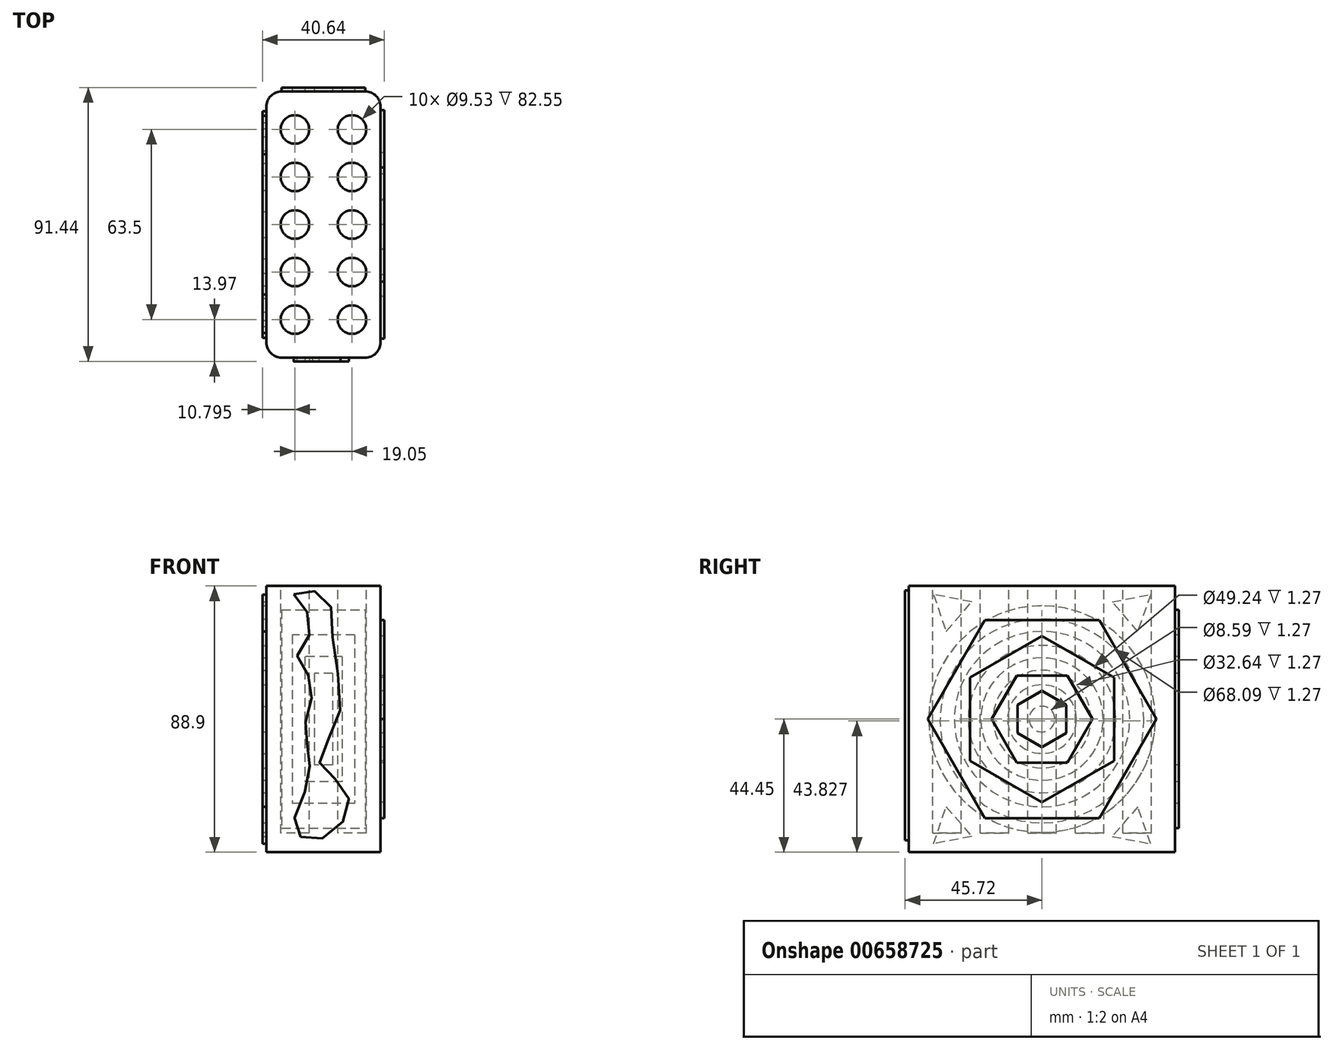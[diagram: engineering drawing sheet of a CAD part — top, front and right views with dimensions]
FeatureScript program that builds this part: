
annotation { "Feature Type Name" : "Feature", "Feature Type Description" : "" }
export const myFeature = defineFeature(function(context is Context, id is Id, definition is map)
    precondition{}
    {
        {
            var Q0;
            Q0=qCreatedBy(makeId("Right.planeOp"),FACE);
            var sketch = newSketch(context, id + "F0", { "sketchPlane" : qUnion([Q0])});
            skLineSegment(sketch, "E0.bottom", {"start": v(-44.45, 44.45) * mm, "end": v(44.45, 44.45) * mm});
            skLineSegment(sketch, "E0.top", {"start": v(-44.45, -44.45) * mm, "end": v(44.45, -44.45) * mm});
            skLineSegment(sketch, "E0.left", {"start": v(-44.45, 44.45) * mm, "end": v(-44.45, -44.45) * mm});
            skLineSegment(sketch, "E0.right", {"start": v(44.45, 44.45) * mm, "end": v(44.45, -44.45) * mm});
            skPoint(sketch, "E0.middle", {"position": v(0, 0) * mm});
            skSolve(sketch);
        }
        {
            var Q0;
            Q0=qSketchRegion(id+"F0",true);
            extrude(context, id + "F1", {"entities" : qUnion([Q0]), "endBound" : BoundingType.SYMMETRIC, "depth" : 38.1 * mm, "offsetDistance" : 25.4 * mm});
        }
        {
            var Q0;
            Q0=makeQuery(id+"F1.opExtrude","SWEPT_FACE",FACE,{"disambiguationData":[OSD([sQuery(id+"F0.wireOp",EDGE,"E0.bottom")])]});
            var sketch = newSketch(context, id + "F2", { "sketchPlane" : qUnion([Q0])});
            skCircle(sketch, "E1", {"center": v(-9.52, -31.75) * mm, "radius": 4.76 * mm});
            skCircle(sketch, "E2", {"center": v(-9.52, 0) * mm, "radius": 4.76 * mm});
            skCircle(sketch, "E3", {"center": v(-9.52, -15.88) * mm, "radius": 4.76 * mm});
            skCircle(sketch, "E4", {"center": v(-9.52, 15.88) * mm, "radius": 4.76 * mm});
            skCircle(sketch, "E5", {"center": v(-9.52, 31.75) * mm, "radius": 4.76 * mm});
            skCircle(sketch, "E6.MirrorC", {"center": v(9.52, 0) * mm, "radius": 4.76 * mm});
            skCircle(sketch, "E7.MirrorC", {"center": v(9.52, -31.75) * mm, "radius": 4.76 * mm});
            skCircle(sketch, "E8.MirrorC", {"center": v(9.52, -15.88) * mm, "radius": 4.76 * mm});
            skCircle(sketch, "E9.MirrorC", {"center": v(9.52, 15.88) * mm, "radius": 4.76 * mm});
            skCircle(sketch, "E10.MirrorC", {"center": v(9.52, 31.75) * mm, "radius": 4.76 * mm});
            skSolve(sketch);
        }
        {
            var Q0;
            Q0=qSketchRegion(id+"F2",true);
            extrude(context, id + "F3", {"entities" : qUnion([Q0]), "operationType" : NewBodyOperationType.REMOVE, "oppositeDirection" : true, "depth" : 82.55 * mm, "offsetDistance" : 25.4 * mm});
        }
        {
            var Q0;
            Q0=makeQuery(id+"F1.opExtrude","CAP_EDGE",EDGE,{"disambiguationData":[OSD([sQuery(id+"F0.wireOp",EDGE,"E0.left")])],"isStart":false});
            var Q1;
            Q1=makeQuery(id+"F1.opExtrude","CAP_EDGE",EDGE,{"disambiguationData":[OSD([sQuery(id+"F0.wireOp",EDGE,"E0.right")])],"isStart":false});
            var Q2;
            Q2=makeQuery(id+"F1.opExtrude","CAP_EDGE",EDGE,{"disambiguationData":[OSD([sQuery(id+"F0.wireOp",EDGE,"E0.right")])],"isStart":true});
            var Q3;
            Q3=makeQuery(id+"F1.opExtrude","CAP_EDGE",EDGE,{"disambiguationData":[OSD([sQuery(id+"F0.wireOp",EDGE,"E0.left")])],"isStart":true});
            fillet(context, id + "F4", {"entities" : qUnion([Q0, Q1, Q2, Q3]), "radius" : 5.08 * mm, "tangentPropagation" : true, "allowEdgeOverflow" : false});
        }
        {
            var Q0;
            Q0=makeQuery(id+"F1.opExtrude","CAP_FACE",FACE,{"disambiguationData":[OSD([sQuery(id+"F0.wireOp",EDGE,"E0.bottom"),sQuery(id+"F0.wireOp",EDGE,"E0.top"),sQuery(id+"F0.wireOp",EDGE,"E0.left"),sQuery(id+"F0.wireOp",EDGE,"E0.right")])],"isStart":false});
            var sketch = newSketch(context, id + "F5", { "sketchPlane" : qUnion([Q0])});
            skCircle(sketch, "E11.cCircle", {"center": v(0, 0) * mm, "radius": 8.15 * mm, "construction": true});
            skLineSegment(sketch, "E11.0", {"start": v(-8.15, -4.7) * mm, "end": v(-8.15, 4.7) * mm});
            skLineSegment(sketch, "E11.1", {"start": v(-8.15, 4.7) * mm, "end": v(0, 9.4) * mm});
            skLineSegment(sketch, "E11.2", {"start": v(0, 9.4) * mm, "end": v(8.15, 4.7) * mm});
            skLineSegment(sketch, "E11.3", {"start": v(8.15, 4.7) * mm, "end": v(8.15, -4.7) * mm});
            skLineSegment(sketch, "E11.4", {"start": v(8.15, -4.7) * mm, "end": v(0, -9.4) * mm});
            skLineSegment(sketch, "E11.5", {"start": v(0, -9.4) * mm, "end": v(-8.15, -4.7) * mm});
            skPoint(sketch, "E11.0.midPoint", {"position": v(-8.15, 0) * mm});
            skCircle(sketch, "E12.cCircle", {"center": v(0, 0) * mm, "radius": 14.58 * mm, "construction": true});
            skLineSegment(sketch, "E12.0", {"start": v(8.42, -14.58) * mm, "end": v(-8.42, -14.58) * mm});
            skLineSegment(sketch, "E12.1", {"start": v(-8.42, -14.58) * mm, "end": v(-16.84, 0) * mm});
            skLineSegment(sketch, "E12.2", {"start": v(-16.84, 0) * mm, "end": v(-8.42, 14.58) * mm});
            skLineSegment(sketch, "E12.3", {"start": v(-8.42, 14.58) * mm, "end": v(8.42, 14.58) * mm});
            skLineSegment(sketch, "E12.4", {"start": v(8.42, 14.58) * mm, "end": v(16.84, 0) * mm});
            skLineSegment(sketch, "E12.5", {"start": v(16.84, 0) * mm, "end": v(8.42, -14.58) * mm});
            skPoint(sketch, "E12.0.midPoint", {"position": v(0, -14.58) * mm});
            skCircle(sketch, "E13.cCircle", {"center": v(0, 0) * mm, "radius": 24.04 * mm, "construction": true});
            skLineSegment(sketch, "E13.0", {"start": v(-24.04, -13.88) * mm, "end": v(-24.04, 13.88) * mm});
            skLineSegment(sketch, "E13.1", {"start": v(-24.04, 13.88) * mm, "end": v(0, 27.76) * mm});
            skLineSegment(sketch, "E13.2", {"start": v(0, 27.76) * mm, "end": v(24.04, 13.88) * mm});
            skLineSegment(sketch, "E13.3", {"start": v(24.04, 13.88) * mm, "end": v(24.04, -13.88) * mm});
            skLineSegment(sketch, "E13.4", {"start": v(24.04, -13.88) * mm, "end": v(0, -27.76) * mm});
            skLineSegment(sketch, "E13.5", {"start": v(0, -27.76) * mm, "end": v(-24.04, -13.88) * mm});
            skPoint(sketch, "E13.0.midPoint", {"position": v(-24.04, 0) * mm});
            skCircle(sketch, "E14.cCircle", {"center": v(0, 0) * mm, "radius": 33.06 * mm, "construction": true});
            skLineSegment(sketch, "E14.0", {"start": v(19.08, -33.06) * mm, "end": v(-19.08, -33.06) * mm});
            skLineSegment(sketch, "E14.1", {"start": v(-19.08, -33.06) * mm, "end": v(-38.17, 0) * mm});
            skLineSegment(sketch, "E14.2", {"start": v(-38.17, 0) * mm, "end": v(-19.08, 33.06) * mm});
            skLineSegment(sketch, "E14.3", {"start": v(-19.08, 33.06) * mm, "end": v(19.08, 33.06) * mm});
            skLineSegment(sketch, "E14.4", {"start": v(19.08, 33.06) * mm, "end": v(38.17, 0) * mm});
            skLineSegment(sketch, "E14.5", {"start": v(38.17, 0) * mm, "end": v(19.08, -33.06) * mm});
            skPoint(sketch, "E14.0.midPoint", {"position": v(0, -33.06) * mm});
            skSolve(sketch);
        }
        {
            var Q0;
            Q0=makeQuery(id+"F5.imprint","IMPRINT",FACE,{"disambiguationData":[TD([[makeQuery(id+"F5.imprint","IMPRINT",EDGE,{"derivedFrom":sQuery(id+"F5.wireOp",EDGE,"E11.0")}),1.0]])]});
            var Q1;
            Q1=makeQuery(id+"F5.imprint","IMPRINT",FACE,{"disambiguationData":[TD([[makeQuery(id+"F5.imprint","IMPRINT",EDGE,{"derivedFrom":sQuery(id+"F5.wireOp",EDGE,"E13.0")}),1.0]])]});
            extrude(context, id + "F6", {"entities" : qUnion([Q0, Q1]), "operationType" : NewBodyOperationType.ADD, "depth" : 1.27 * mm, "offsetDistance" : 25.4 * mm});
        }
        {
            var Q0;
            Q0=makeQuery(id+"F1.opExtrude","CAP_FACE",FACE,{"disambiguationData":[OSD([sQuery(id+"F0.wireOp",EDGE,"E0.bottom"),sQuery(id+"F0.wireOp",EDGE,"E0.top"),sQuery(id+"F0.wireOp",EDGE,"E0.left"),sQuery(id+"F0.wireOp",EDGE,"E0.right")])],"isStart":true});
            var sketch = newSketch(context, id + "F7", { "sketchPlane" : qUnion([Q0])});
            skCircle(sketch, "E15", {"center": v(0, 0) * mm, "radius": 4.3 * mm});
            skCircle(sketch, "E16", {"center": v(0, 0) * mm, "radius": 11.47 * mm});
            skCircle(sketch, "E17", {"center": v(0, 0) * mm, "radius": 16.32 * mm});
            skCircle(sketch, "E18", {"center": v(0, 0) * mm, "radius": 20.43 * mm});
            skCircle(sketch, "E19", {"center": v(0, 0) * mm, "radius": 24.62 * mm});
            skCircle(sketch, "E20", {"center": v(0, 0) * mm, "radius": 29.27 * mm});
            skCircle(sketch, "E21", {"center": v(0, -0.62) * mm, "radius": 34.04 * mm});
            skCircle(sketch, "E22", {"center": v(0, 0) * mm, "radius": 37.84 * mm});
            skSolve(sketch);
        }
        {
            var Q0;
            Q0=makeQuery(id+"F7.imprint","IMPRINT",FACE,{"disambiguationData":[TD([[makeQuery(id+"F7.imprint","IMPRINT",EDGE,{"derivedFrom":sQuery(id+"F7.wireOp",EDGE,"E15")}),-1.0]])]});
            var Q1;
            Q1=makeQuery(id+"F7.imprint","IMPRINT",FACE,{"disambiguationData":[TD([[makeQuery(id+"F7.imprint","IMPRINT",EDGE,{"derivedFrom":sQuery(id+"F7.wireOp",EDGE,"E17")}),-1.0]])]});
            var Q2;
            Q2=makeQuery(id+"F7.imprint","IMPRINT",FACE,{"disambiguationData":[TD([[makeQuery(id+"F7.imprint","IMPRINT",EDGE,{"derivedFrom":sQuery(id+"F7.wireOp",EDGE,"E19")}),-1.0]])]});
            var Q3;
            Q3=makeQuery(id+"F7.imprint","IMPRINT",FACE,{"disambiguationData":[TD([[makeQuery(id+"F7.imprint","IMPRINT",EDGE,{"derivedFrom":sQuery(id+"F7.wireOp",EDGE,"E21")}),-1.0]])]});
            extrude(context, id + "F8", {"entities" : qUnion([Q0, Q1, Q2, Q3]), "operationType" : NewBodyOperationType.ADD, "depth" : 1.27 * mm, "offsetDistance" : 25.4 * mm});
        }
        {
            var Q0;
            {var subQ0=sQuery(id+"F0.wireOp",EDGE,"E0.right");var subQ1=sQuery(id+"F0.wireOp",EDGE,"E0.bottom");var subQ2=sQuery(id+"F0.wireOp",EDGE,"E0.top");var subQ3=sQuery(id+"F0.wireOp",EDGE,"E0.left");Q0=makeQuery(id+"F8.boolean.opBoolean","SPLIT",FACE,{"disambiguationData":[TD([makeQuery(id+"F1.opExtrude","SWEPT_FACE",FACE,{"disambiguationData":[OSD([subQ1])]})])],"derivedFrom":makeQuery(id+"F1.opExtrude","CAP_FACE",FACE,{"disambiguationData":[OSD([subQ1,subQ2,subQ3,subQ0])],"isStart":true})});}
            var sketch = newSketch(context, id + "F9", { "sketchPlane" : qUnion([Q0])});
            skCircle(sketch, "E23.cCircle", {"center": v(30.56, 36.7) * mm, "radius": 3.76 * mm, "construction": true});
            skLineSegment(sketch, "E23.0", {"start": v(36.24, 41.63) * mm, "end": v(32, 29.3) * mm});
            skLineSegment(sketch, "E23.1", {"start": v(32, 29.3) * mm, "end": v(23.44, 39.15) * mm});
            skLineSegment(sketch, "E23.2", {"start": v(23.44, 39.15) * mm, "end": v(36.24, 41.63) * mm});
            skPoint(sketch, "E23.0.midPoint", {"position": v(34.12, 35.47) * mm});
            skCircle(sketch, "E24.MirrorC", {"center": v(-30.56, 36.7) * mm, "radius": 3.76 * mm, "construction": true});
            skLineSegment(sketch, "E25.MirrorCS", {"start": v(-36.24, 41.63) * mm, "end": v(-32, 29.3) * mm});
            skLineSegment(sketch, "E26.MirrorCS", {"start": v(-23.44, 39.15) * mm, "end": v(-36.24, 41.63) * mm});
            skLineSegment(sketch, "E27.MirrorCS", {"start": v(-32, 29.3) * mm, "end": v(-23.44, 39.15) * mm});
            skPoint(sketch, "E28.MirrorP", {"position": v(-34.12, 35.47) * mm});
            skLineSegment(sketch, "E29.MirrorCS", {"start": v(-36.24, -41.63) * mm, "end": v(-32, -29.3) * mm});
            skCircle(sketch, "E30.MirrorC", {"center": v(-30.56, -36.7) * mm, "radius": 3.76 * mm, "construction": true});
            skLineSegment(sketch, "E31.MirrorCS", {"start": v(23.44, -39.15) * mm, "end": v(36.24, -41.63) * mm});
            skLineSegment(sketch, "E32.MirrorCS", {"start": v(-32, -29.3) * mm, "end": v(-23.44, -39.15) * mm});
            skLineSegment(sketch, "E33.MirrorCS", {"start": v(32, -29.3) * mm, "end": v(23.44, -39.15) * mm});
            skCircle(sketch, "E34.MirrorC", {"center": v(30.56, -36.7) * mm, "radius": 3.76 * mm, "construction": true});
            skLineSegment(sketch, "E35.MirrorCS", {"start": v(-23.44, -39.15) * mm, "end": v(-36.24, -41.63) * mm});
            skLineSegment(sketch, "E36.MirrorCS", {"start": v(36.24, -41.63) * mm, "end": v(32, -29.3) * mm});
            skPoint(sketch, "E37.MirrorP", {"position": v(34.12, -35.47) * mm});
            skPoint(sketch, "E38.MirrorP", {"position": v(-34.12, -35.47) * mm});
            skSolve(sketch);
        }
        {
            var Q0;
            Q0=makeQuery(id+"F9.imprint","IMPRINT",FACE,{"disambiguationData":[TD([[makeQuery(id+"F9.imprint","IMPRINT",EDGE,{"derivedFrom":sQuery(id+"F9.wireOp",EDGE,"E25.MirrorCS")}),1.0]])]});
            var Q1;
            Q1=makeQuery(id+"F9.imprint","IMPRINT",FACE,{"disambiguationData":[TD([[makeQuery(id+"F9.imprint","IMPRINT",EDGE,{"derivedFrom":sQuery(id+"F9.wireOp",EDGE,"E23.0")}),-1.0]])]});
            var Q2;
            Q2=makeQuery(id+"F9.imprint","IMPRINT",FACE,{"disambiguationData":[TD([[makeQuery(id+"F9.imprint","IMPRINT",EDGE,{"derivedFrom":sQuery(id+"F9.wireOp",EDGE,"E31.MirrorCS")}),1.0]])]});
            var Q3;
            Q3=makeQuery(id+"F9.imprint","IMPRINT",FACE,{"disambiguationData":[TD([[makeQuery(id+"F9.imprint","IMPRINT",EDGE,{"derivedFrom":sQuery(id+"F9.wireOp",EDGE,"E29.MirrorCS")}),-1.0]])]});
            extrude(context, id + "F10", {"entities" : qUnion([Q0, Q1, Q2, Q3]), "operationType" : NewBodyOperationType.ADD, "depth" : 1.27 * mm, "offsetDistance" : 25.4 * mm});
        }
        {
            var Q0;
            Q0=makeQuery(id+"F1.opExtrude","SWEPT_FACE",FACE,{"disambiguationData":[OSD([sQuery(id+"F0.wireOp",EDGE,"E0.right")])]});
            var sketch = newSketch(context, id + "F11", { "sketchPlane" : qUnion([Q0])});
            skLineSegment(sketch, "E39.bottom", {"start": v(13.97, -36.45) * mm, "end": v(-13.97, -36.45) * mm});
            skLineSegment(sketch, "E39.top", {"start": v(13.97, 36.45) * mm, "end": v(-13.97, 36.45) * mm});
            skLineSegment(sketch, "E39.left", {"start": v(13.97, -36.45) * mm, "end": v(13.97, 36.45) * mm});
            skLineSegment(sketch, "E39.right", {"start": v(-13.97, -36.45) * mm, "end": v(-13.97, 36.45) * mm});
            skPoint(sketch, "E39.middle", {"position": v(0, 0) * mm});
            skLineSegment(sketch, "E40.bottom", {"start": v(-10.43, 28.1) * mm, "end": v(10.43, 28.1) * mm});
            skLineSegment(sketch, "E40.top", {"start": v(-10.43, -28.1) * mm, "end": v(10.43, -28.1) * mm});
            skLineSegment(sketch, "E40.left", {"start": v(-10.43, 28.1) * mm, "end": v(-10.43, -28.1) * mm});
            skLineSegment(sketch, "E40.right", {"start": v(10.43, 28.1) * mm, "end": v(10.43, -28.1) * mm});
            skLineSegment(sketch, "E41.bottom", {"start": v(-6.26, 20.86) * mm, "end": v(6.26, 20.86) * mm});
            skLineSegment(sketch, "E41.top", {"start": v(-6.26, -20.86) * mm, "end": v(6.26, -20.86) * mm});
            skLineSegment(sketch, "E41.left", {"start": v(-6.26, 20.86) * mm, "end": v(-6.26, -20.86) * mm});
            skLineSegment(sketch, "E41.right", {"start": v(6.26, 20.86) * mm, "end": v(6.26, -20.86) * mm});
            skLineSegment(sketch, "E42.bottom", {"start": v(-3.07, 15.34) * mm, "end": v(3.07, 15.34) * mm});
            skLineSegment(sketch, "E42.top", {"start": v(-3.07, -15.34) * mm, "end": v(3.07, -15.34) * mm});
            skLineSegment(sketch, "E42.left", {"start": v(-3.07, 15.34) * mm, "end": v(-3.07, -15.34) * mm});
            skLineSegment(sketch, "E42.right", {"start": v(3.07, 15.34) * mm, "end": v(3.07, -15.34) * mm});
            skSolve(sketch);
        }
        {
            var Q0;
            Q0=makeQuery(id+"F11.imprint","IMPRINT",FACE,{"disambiguationData":[TD([[makeQuery(id+"F11.imprint","IMPRINT",EDGE,{"derivedFrom":sQuery(id+"F11.wireOp",EDGE,"E39.bottom")}),-1.0]])]});
            var Q1;
            Q1=makeQuery(id+"F11.imprint","IMPRINT",FACE,{"disambiguationData":[TD([[makeQuery(id+"F11.imprint","IMPRINT",EDGE,{"derivedFrom":sQuery(id+"F11.wireOp",EDGE,"E41.bottom")}),-1.0]])]});
            extrude(context, id + "F12", {"entities" : qUnion([Q0, Q1]), "operationType" : NewBodyOperationType.ADD, "depth" : 1.27 * mm, "offsetDistance" : 25.4 * mm});
        }
        {
            var Q0;
            Q0=makeQuery(id+"F1.opExtrude","SWEPT_FACE",FACE,{"disambiguationData":[OSD([sQuery(id+"F0.wireOp",EDGE,"E0.left")])]});
            var sketch = newSketch(context, id + "F13", { "sketchPlane" : qUnion([Q0])});
            skFitSpline(sketch, "E43", {"points": [v(-9.94, 41.73) * mm, v(-3.56, 32.28) * mm, v(-8.71, 21.35) * mm, v(-3.8, 12.15) * mm, v(-5.9, 0) * mm, v(-5.15, -9.7) * mm, v(-5.4, -21.84) * mm, v(-9.82, -35.83) * mm, v(-3.56, -40.5) * mm, v(7.12, -33.26) * mm, v(6.75, -22.7) * mm, v(-1.35, -14.48) * mm, v(4.9, 0) * mm, v(3.07, 27.12) * mm, v(0, 41.48) * mm, v(-9.94, 41.73) * mm]});
            skSolve(sketch);
        }
        {
            var Q0;
            Q0=makeQuery(id+"F13.imprint","IMPRINT",FACE,{"disambiguationData":[TD([[makeQuery(id+"F13.imprint","IMPRINT",EDGE,{"derivedFrom":sQuery(id+"F13.wireOp",EDGE,"E43")}),1.0]])]});
            extrude(context, id + "F14", {"entities" : qUnion([Q0]), "operationType" : NewBodyOperationType.ADD, "depth" : 1.27 * mm, "offsetDistance" : 25.4 * mm});
        }
    });
